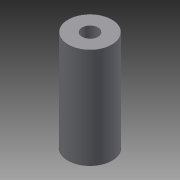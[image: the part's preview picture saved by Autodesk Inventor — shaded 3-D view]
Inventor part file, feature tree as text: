
AUTODESK INVENTOR PART (.ipt)
format: ipt  version: 2014 (Build 180170000, 170)  size: 70,144 bytes
history: native  units: mm
features: other x1, extrude x1, sketch x1
ambient origin geometry x8: Origin, YZ Plane, XZ Plane, XY Plane, X Axis, Y Axis, Z Axis, Center Point
bodies: Body1 (feature_tree)
feature tree (3):
  other  "Твердое тело1"
  extrude  "Выдавливание1"  Depth=2.5mm
  sketch  "Эскиз1"
